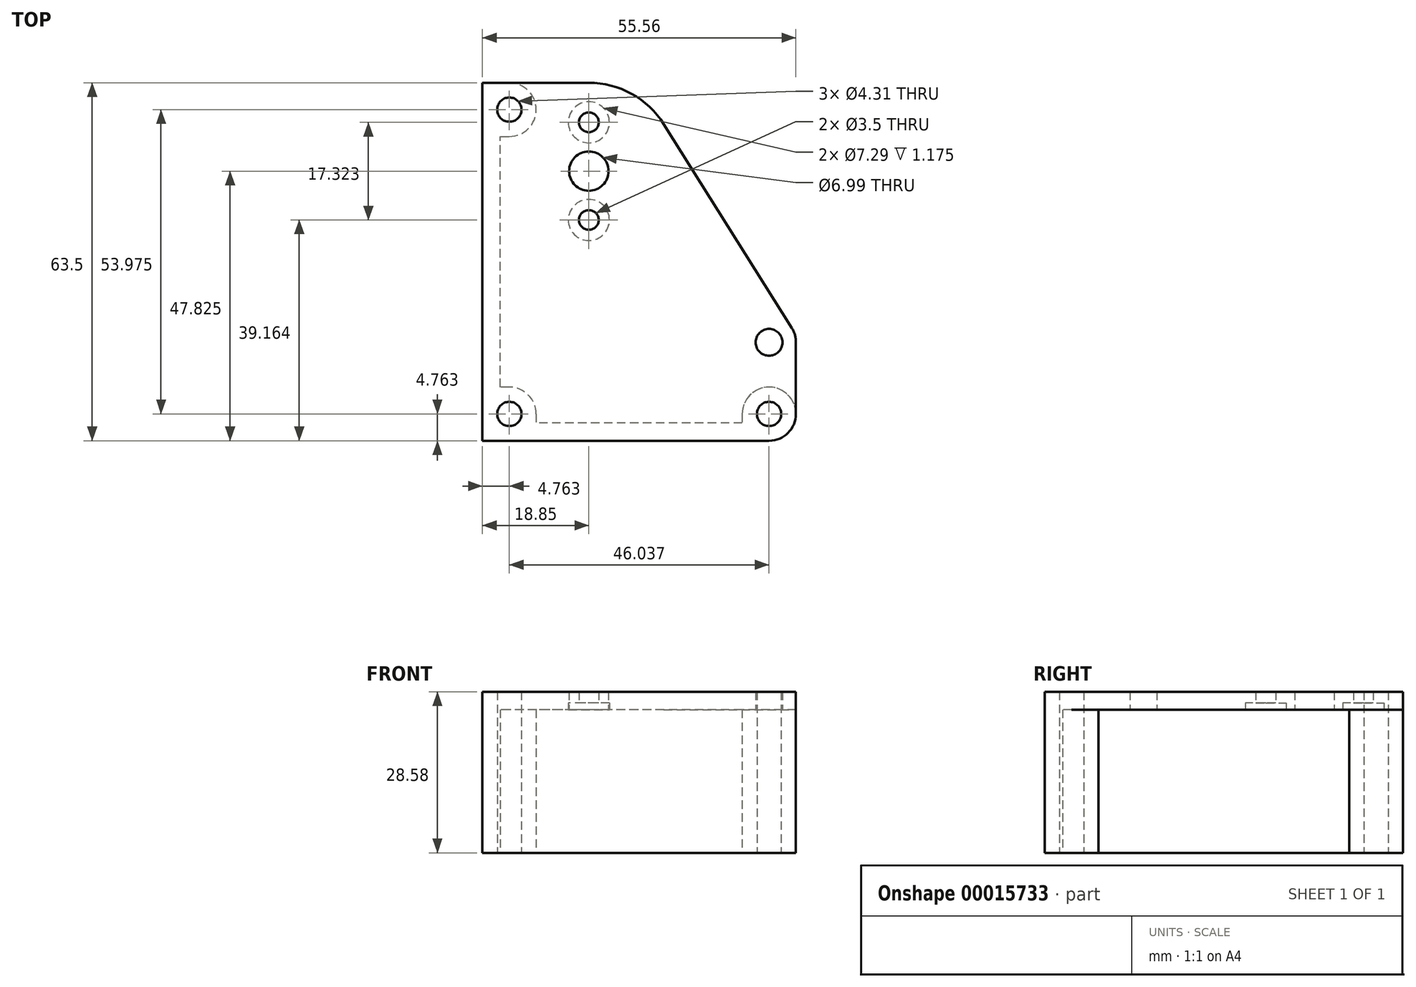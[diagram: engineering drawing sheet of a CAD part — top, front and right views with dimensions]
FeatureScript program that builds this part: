
annotation { "Feature Type Name" : "Feature", "Feature Type Description" : "" }
export const myFeature = defineFeature(function(context is Context, id is Id, definition is map)
    precondition{}
    {
        {
            var Q0;
            Q0=qCreatedBy(makeId("Top.planeOp"),FACE);
            var sketch = newSketch(context, id + "F0", { "sketchPlane" : qUnion([Q0])});
            skLineSegment(sketch, "E0.bottom", {"start": v(0, 0) * mm, "end": v(50.8, 0) * mm});
            skLineSegment(sketch, "E0.left", {"start": v(0, 0) * mm, "end": v(0, 63.5) * mm});
            skLineSegment(sketch, "E1", {"start": v(4.76, 0) * mm, "end": v(4.76, 4.76) * mm, "construction": true});
            skLineSegment(sketch, "E2", {"start": v(4.76, 4.76) * mm, "end": v(0, 4.76) * mm, "construction": true});
            skCircle(sketch, "E3", {"center": v(4.76, 4.76) * mm, "radius": 2.15 * mm});
            skCircle(sketch, "E4", {"center": v(50.8, 4.76) * mm, "radius": 2.15 * mm});
            skArc(sketch, "E5", {"start": v(50.8, 0) * mm, "mid": v(54.17, 8.13) * mm, "end": v(46.04, 4.76) * mm});
            skLineSegment(sketch, "E6", {"start": v(46.04, 4.76) * mm, "end": v(46.04, 3.18) * mm});
            skLineSegment(sketch, "E7", {"start": v(46.04, 3.18) * mm, "end": v(9.53, 3.17) * mm});
            skLineSegment(sketch, "E8", {"start": v(9.53, 4.76) * mm, "end": v(9.53, 3.17) * mm});
            skArc(sketch, "E9", {"start": v(9.53, 4.76) * mm, "mid": v(8.13, 8.13) * mm, "end": v(4.76, 9.52) * mm});
            skLineSegment(sketch, "E10", {"start": v(46.04, 3.18) * mm, "end": v(46.04, 0) * mm, "construction": true});
            skLineSegment(sketch, "E11", {"start": v(4.76, 9.52) * mm, "end": v(3.18, 9.52) * mm});
            skLineSegment(sketch, "E12", {"start": v(3.18, 9.52) * mm, "end": v(3.18, 53.98) * mm});
            skLineSegment(sketch, "E13", {"start": v(0, 63.5) * mm, "end": v(4.76, 63.5) * mm});
            skArc(sketch, "E14", {"start": v(4.76, 53.97) * mm, "mid": v(9.52, 58.74) * mm, "end": v(4.76, 63.5) * mm});
            skLineSegment(sketch, "E15", {"start": v(3.17, 53.98) * mm, "end": v(4.76, 53.98) * mm});
            skCircle(sketch, "E16", {"center": v(4.76, 58.74) * mm, "radius": 2.15 * mm});
            skSolve(sketch);
        }
        {
            var Q0;
            Q0=qSketchRegion(id+"F0",true);
            extrude(context, id + "F1", {"entities" : qUnion([Q0]), "depth" : 25.4 * mm});
        }
        {
            var Q0;
            Q0=makeQuery(id+"F1.opExtrude","CAP_FACE",FACE,{"disambiguationData":[OSD([sQuery(id+"F0.wireOp",EDGE,"E0.bottom"),sQuery(id+"F0.wireOp",EDGE,"E0.left"),sQuery(id+"F0.wireOp",EDGE,"E3"),sQuery(id+"F0.wireOp",EDGE,"E4"),sQuery(id+"F0.wireOp",EDGE,"E5"),sQuery(id+"F0.wireOp",EDGE,"E6"),sQuery(id+"F0.wireOp",EDGE,"E7"),sQuery(id+"F0.wireOp",EDGE,"E8"),sQuery(id+"F0.wireOp",EDGE,"E9"),sQuery(id+"F0.wireOp",EDGE,"E11"),sQuery(id+"F0.wireOp",EDGE,"E12"),sQuery(id+"F0.wireOp",EDGE,"E13"),sQuery(id+"F0.wireOp",EDGE,"E14"),sQuery(id+"F0.wireOp",EDGE,"E15"),sQuery(id+"F0.wireOp",EDGE,"E16")])],"isStart":false});
            var sketch = newSketch(context, id + "F2", { "sketchPlane" : qUnion([Q0])});
            skLineSegment(sketch, "E17", {"start": v(55.56, 4.76) * mm, "end": v(55.56, 17.46) * mm});
            skLineSegment(sketch, "E18.bottom", {"start": v(50.8, 0) * mm, "end": v(0, 0) * mm});
            skLineSegment(sketch, "E18.top", {"start": v(18.85, 63.5) * mm, "end": v(0, 63.5) * mm});
            skLineSegment(sketch, "E18.right", {"start": v(0, 0) * mm, "end": v(0, 63.5) * mm});
            skArc(sketch, "E19", {"start": v(55.56, 17.46) * mm, "mid": v(55.38, 18.78) * mm, "end": v(54.83, 20) * mm});
            skArc(sketch, "E20", {"start": v(32.13, 56.16) * mm, "mid": v(26.43, 61.54) * mm, "end": v(18.85, 63.5) * mm});
            skCircle(sketch, "E21", {"center": v(18.85, 47.83) * mm, "radius": 12.5 * mm, "construction": true});
            skLineSegment(sketch, "E22", {"start": v(18.85, 47.83) * mm, "end": v(6.35, 47.83) * mm, "construction": true});
            skLineSegment(sketch, "E23", {"start": v(6.35, 47.83) * mm, "end": v(3.18, 47.83) * mm, "construction": true});
            skLineSegment(sketch, "E24", {"start": v(50.8, 4.76) * mm, "end": v(50.8, 17.46) * mm, "construction": true});
            skLineSegment(sketch, "E25", {"start": v(32.13, 56.16) * mm, "end": v(54.83, 20) * mm});
            skCircle(sketch, "E26", {"center": v(4.76, 58.74) * mm, "radius": 2.15 * mm});
            skCircle(sketch, "E27", {"center": v(50.8, 4.76) * mm, "radius": 2.15 * mm});
            skCircle(sketch, "E28", {"center": v(4.76, 4.76) * mm, "radius": 2.15 * mm});
            skCircle(sketch, "E29", {"center": v(50.8, 17.46) * mm, "radius": 2.38 * mm});
            skLineSegment(sketch, "E30", {"start": v(18.85, 56.49) * mm, "end": v(18.85, 39.16) * mm, "construction": true});
            skCircle(sketch, "E31", {"center": v(18.85, 47.83) * mm, "radius": 3.5 * mm});
            skCircle(sketch, "E32", {"center": v(18.85, 56.49) * mm, "radius": 1.75 * mm});
            skCircle(sketch, "E33", {"center": v(18.85, 39.16) * mm, "radius": 1.75 * mm});
            skSolve(sketch);
        }
        {
            var Q0;
            {var subQ1=sQuery(id+"F2.wireOp",EDGE,"E17");Q0=makeQuery(id+"F2.imprint","IMPRINT",FACE,{"disambiguationData":[TD([[makeQuery(id+"F2.imprint","IMPRINT",EDGE,{"derivedFrom":subQ1}),1.0]])]});}
            var Q1;
            {var subQ0=sQuery(id+"F2.wireOp",EDGE,"E18.bottom");Q1=makeQuery(id+"F2.imprint","IMPRINT",FACE,{"disambiguationData":[TD([[makeQuery(id+"F2.imprint","IMPRINT",EDGE,{"derivedFrom":subQ0}),1.0]])]});}
            extrude(context, id + "F3", {"entities" : qUnion([Q0, Q1]), "operationType" : NewBodyOperationType.ADD, "depth" : 3.17 * mm});
        }
        {
            var Q0;
            Q0=makeQuery(id+"F3.opExtrude","CAP_FACE",FACE,{"disambiguationData":[OSD([sQuery(id+"F0.wireOp",EDGE,"E5"),sQuery(id+"F2.wireOp",EDGE,"E17"),sQuery(id+"F2.wireOp",EDGE,"E18.bottom"),sQuery(id+"F2.wireOp",EDGE,"E18.top"),sQuery(id+"F2.wireOp",EDGE,"E18.right"),sQuery(id+"F2.wireOp",EDGE,"E19"),sQuery(id+"F2.wireOp",EDGE,"E20"),sQuery(id+"F2.wireOp",EDGE,"E25"),sQuery(id+"F2.wireOp",EDGE,"E26"),sQuery(id+"F2.wireOp",EDGE,"E27"),sQuery(id+"F2.wireOp",EDGE,"E28"),sQuery(id+"F2.wireOp",EDGE,"E29"),sQuery(id+"F2.wireOp",EDGE,"E31"),sQuery(id+"F2.wireOp",EDGE,"E32"),sQuery(id+"F2.wireOp",EDGE,"E33")])],"isStart":false});
            cPlane(context, id + "F4", {"entities" : qUnion([Q0]), "cplaneType" : CPlaneType.OFFSET, "offset" : 2 * mm, "oppositeDirection" : true, "width" : 152.4 * mm, "height" : 152.4 * mm});
        }
        {
            var Q0;
            Q0=makeQuery(id+"F3.opExtrude","CAP_FACE",FACE,{"disambiguationData":[OSD([sQuery(id+"F0.wireOp",EDGE,"E5"),sQuery(id+"F2.wireOp",EDGE,"E17"),sQuery(id+"F2.wireOp",EDGE,"E18.bottom"),sQuery(id+"F2.wireOp",EDGE,"E18.top"),sQuery(id+"F2.wireOp",EDGE,"E18.right"),sQuery(id+"F2.wireOp",EDGE,"E19"),sQuery(id+"F2.wireOp",EDGE,"E20"),sQuery(id+"F2.wireOp",EDGE,"E25"),sQuery(id+"F2.wireOp",EDGE,"E26"),sQuery(id+"F2.wireOp",EDGE,"E27"),sQuery(id+"F2.wireOp",EDGE,"E28"),sQuery(id+"F2.wireOp",EDGE,"E29"),sQuery(id+"F2.wireOp",EDGE,"E31"),sQuery(id+"F2.wireOp",EDGE,"E32"),sQuery(id+"F2.wireOp",EDGE,"E33")])],"isStart":true});
            var sketch = newSketch(context, id + "F5", { "sketchPlane" : qUnion([Q0])});
            skCircle(sketch, "E34", {"center": v(18.85, -39.16) * mm, "radius": 3.64 * mm});
            skCircle(sketch, "E35", {"center": v(18.85, -56.49) * mm, "radius": 3.64 * mm});
            skSolve(sketch);
        }
        {
            var Q0;
            Q0 = qSketchRegion(id + "F5", true);
            var Q1;
            Q1=qCreatedBy(id+"F4.planeOp",FACE);
            extrude(context, id + "F6", {"entities" : qUnion([Q0]), "operationType" : NewBodyOperationType.REMOVE, "endBound" : BoundingType.UP_TO_SURFACE, "oppositeDirection" : true, "endBoundEntityFace" : qUnion([Q1]), "depth" : 25.4 * mm});
        }
    });
